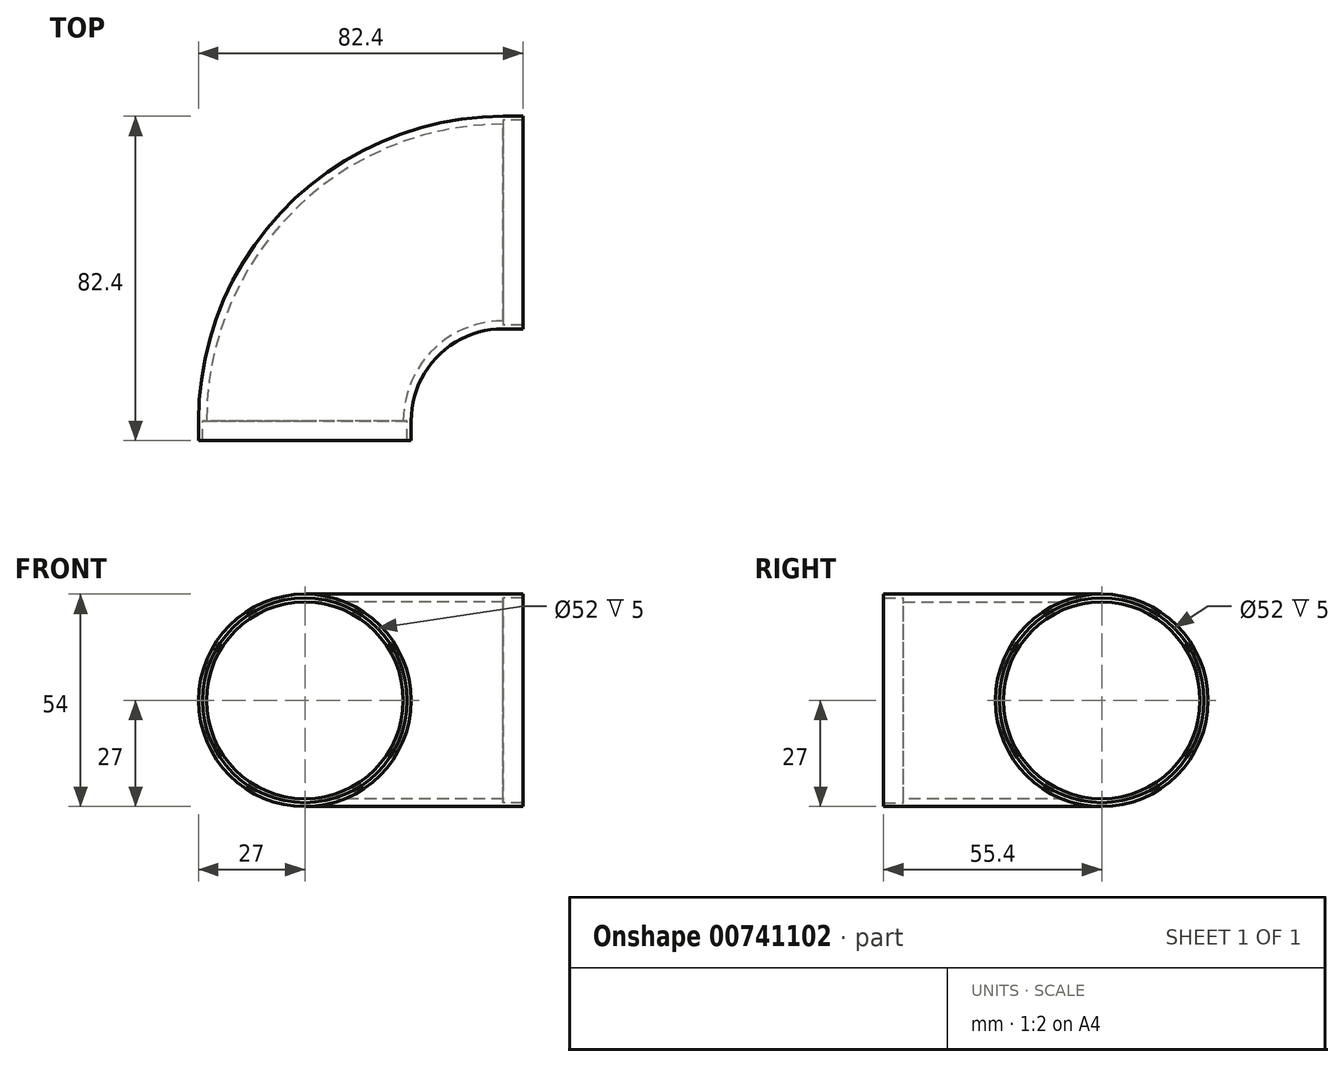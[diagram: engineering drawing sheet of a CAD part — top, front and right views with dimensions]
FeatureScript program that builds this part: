
annotation { "Feature Type Name" : "Feature", "Feature Type Description" : "" }
export const myFeature = defineFeature(function(context is Context, id is Id, definition is map)
    precondition{}
    {
        {
            var Q0;
            Q0=qCreatedBy(makeId("Front.planeOp"),FACE);
            var sketch = newSketch(context, id + "F0", { "sketchPlane" : qUnion([Q0])});
            skCircle(sketch, "E0", {"center": v(0, 0) * mm, "radius": 27 * mm});
            skCircle(sketch, "E1", {"center": v(0, 0) * mm, "radius": 25 * mm});
            skLineSegment(sketch, "E2", {"start": v(50.4, 43.13) * mm, "end": v(50.4, -62.12) * mm, "construction": true});
            skSolve(sketch);
        }
        {
            var Q0;
            Q0=makeQuery(id+"F0.imprint","IMPRINT",FACE,{"disambiguationData":[TD([[makeQuery(id+"F0.imprint","IMPRINT",EDGE,{"derivedFrom":sQuery(id+"F0.wireOp",EDGE,"E0")}),1.0]])]});
            var Q1;
            Q1=sQuery(id+"F0.wireOp",EDGE,"E2");
            revolve(context, id + "F1", {"surfaceOperationType" : NewSurfaceOperationType.NEW, "entities" : qUnion([Q0]), "axis" : qUnion([Q1]), "revolveType" : RevolveType.ONE_DIRECTION, "angle" : 90 * degree});
        }
        {
            var Q0;
            Q0=qCreatedBy(makeId("Front.planeOp"),FACE);
            var sketch = newSketch(context, id + "F2", { "sketchPlane" : qUnion([Q0])});
            skCircle(sketch, "E3", {"center": v(0, 0) * mm, "radius": 27 * mm});
            skCircle(sketch, "E4", {"center": v(0, 0) * mm, "radius": 26 * mm});
            skSolve(sketch);
        }
        {
            var Q0;
            Q0 = qSketchRegion(id + "F2", true);
            extrude(context, id + "F3", {"entities" : qUnion([Q0]), "operationType" : NewBodyOperationType.ADD, "depth" : 5 * mm, "offsetDistance" : 25 * mm});
        }
        {
            var Q0;
            Q0=makeQuery(id+"F1.opRevolve","CAP_FACE",FACE,{"disambiguationData":[OSD([sQuery(id+"F0.wireOp",EDGE,"E0"),sQuery(id+"F0.wireOp",EDGE,"E1")])],"isStart":false});
            var sketch = newSketch(context, id + "F4", { "sketchPlane" : qUnion([Q0])});
            skCircle(sketch, "E5", {"center": v(50.4, 0) * mm, "radius": 26 * mm});
            skCircle(sketch, "E6", {"center": v(50.4, 0) * mm, "radius": 27 * mm});
            skSolve(sketch);
        }
        {
            var Q0;
            Q0 = qSketchRegion(id + "F4", true);
            extrude(context, id + "F5", {"entities" : qUnion([Q0]), "operationType" : NewBodyOperationType.ADD, "depth" : 5 * mm, "offsetDistance" : 25 * mm});
        }
    });
